# Revit family: 3f_filippi_-_3f_linux_s_ip54_3f_filippi_-_a20726_-_sistema_3f_linux_5p_ip54_l1778
name_source: partatom
category: Lighting Fixtures
units: mm (PartAtom-declared; Revit-internal decimal feet)

## family parameters
Cut with Voids When Loaded = No
Host = Face
Light Source = No
Part Type = Normal
Room Calculation Point = No
Round Connector Dimension = Use Diameter
Shared = No

## types (1)
- 3F Filippi - 3F Linux S IP54
    Apparent Load = 0 VA
    Default Elevation = 1800 mm
    Description = Wired supporting structure for continuous channels, suitable for: lighting units 3F Linux L or transport of electrical lines.

MECHANICAL
Hot-galvanised wired structure, painted in polyester base white, obtained through rolling process, with expanded EPDM rubber profiles.
Transparent polycarbonate IP54 cover element with methacrylate (PMMA) flexible parts.
Dimensions: 1778x64 mm, height 72 mm. Weight 2.59 kg.
IP54 protection degree.
Glow-wire test resistance 650°C.

ELECTRICAL
5-pole through power supply line with with H07Z-U Halogen Free cables (2.5 mm² HT90 cross-section), equipped with quick connection start/end channel terminal blocks, non-reversible, 1 power tower (5P=N/T/1/2/3).
Feeding input on top at the beginning of the structure or at end cap.

INSTALLATION
Ceiling / Suspended.
Attention: to obtain a light system with IP54 protection rating, it is necessary to use 3F Linux L light modules (or alternatively IP54 closing top) + closing terminals.
All accessories dedicated to this product are available on the Catalog and on our website www.3F-Filippi.com.

APPLICATIONS
Dry, dusty indoor environments, subject to occasional water splashes.
Virtually in all environments compatibly with the use of any chemicals which could compromise the use of plastic materials.
Not suitable in environments where chlorine fumes, ligroin, hydrocarbon mixtures, mineral oil vapours or fumes of lubricating emulsions to cool down machine tools are present.
Not suitable for installation on surfaces subject to important vibrations, exposed to weather conditions, on ropes or poles.
For specific applications please contact our technical offices.

WARNING
Luminaire designed for disposal/recycling at end-of-life.
    Height = 72 mm
    Lamp = 0 x
    Length = 1778 mm
    Luminous efficacy = 0 lm/W
    Manufacturer = 3F Filippi
    ModVariant = No
    Model = 3F Filippi - A20726 - Sistema 3F Linux 5P IP54 L1778
    Mounting Place = Ceiling
    Mounting Type = Pendant
    Number of Poles = 1
    OnlyDefault = Yes
    Power Factor = 1
    Product Name = 3F Filippi - 3F Linux S IP54
    Product group = Accessories
    ProductGroupID = 98
    Protection Class = Protection class
    Protection Degree = IP 54
    RLX_Detail_Level = 1
    RLX_Emergency_Light_Flux = 0 lm
    RLX_Emergency_Type = 0
    RLX_Emergency_Type_DB = No
    RlxData = <blob elided: 82429 chars, md5=336d8097>
    Standby Power = 0 W
    System Light Flux = 0 lm
    System Power = 0 W
    Type Comments = Product without accessories
    Type Image = 3ffilippi_3f_linux_s_ip54_l1778.jpg
    URL = http://relux.com
    VarID = ---
    Voltage = 0 V
    Weight = 0.00 kg
    Width = 64 mm

## geometry (parser evidence)
native form markers: Sweep x9
no freeform markers — native parametric forms only
